# Revit family: LAMP_MOODY G2 800 + ROUND FIXED IP55 REFLECTOR
name_source: partatom
category: Luminarias
revit_build: Autodesk Revit 2015 (Build: 20140606_1530(x64)
units: mm (PartAtom-declared; Revit-internal decimal feet)

## types (9) — shared parameters
Altura reflector = 57 mm
Black reflector code = MORFRD100FX55B
Black reflector datasheet = http://www.lamp.es
Black reflector description = MOODY REF RD FX Ø99 BK.
Black reflector finish = Matt black
Black reflector model = MORFRD100FX55B
Cambio de temperatura de color de luz atenuada = <Ninguno>
Comentarios de tipo = Availability of switching reflector colour when placed in a project.
Core datasheet = http://www.lamp.es
Core description = MOODY CORE 500 VWW MFL
Core diameter = 50 mm  [stored 0.164042 ft]
Fabricante = LAMP
Filtro de color = 16777215
Gear = Electronic
IEE = A++
Installation instructions = https://www.lamp.es
Insulation class = II
LED Lifetime = 50.000 L90 B10
Last update = 28/08/2019
Luminaire type = Indoor - Recessed Downlight
Lámpara = COB LED
MacAdam = 3
Manufacturer URL = http://www.lamp.es
Manufacturer country = Spain
Manufacturer name = LAMP
Material Muelle Emp. = LAMP_Acero genérico
Material Reflector Blanco = LAMP_PC Reflector Moody BL
Material Reflector Cobre = LAMP_PC Reflector Moody CO
Material Reflector Negro = LAMP_PC Reflector Moody NG
Material Reflector Plata = LAMP_PC Reflector Moody GR
Material cristal = Cristal
Model explanation = Availability of switching reflector colour when placed in a project.
Plum = 6 W
Power = 5 W
Power Supply = 220-240V 50/60Hz
Product URL = https://www.lamp.es
Protection rating = IP20
Recessed diameter = 95 mm
Reflector diameter = 100 mm  [stored 0.328084 ft]
Total height = 115 mm  [stored 0.377297 ft]
Total weight = 0.25 kg
Type = COB PHILIPS
UGR = 21
White reflector code = MORFRD100FX55W
White reflector datasheet = http://www.lamp.es
White reflector description = MOODY REF RD FX Ø99 WH.
White reflector finish = Matt white
White reflector model = MORFRD100FX55W
Ángulo de inclinación = 90.00°

## per-type parameters (varying)
| type | Archivo de red fotométrica | CRI | Core model | Core product code | Descripción | Efficacy |
| 2700K FLOOD | MO208FL927TB.IES | 90 | MO208FL927TB | MO208FL927TB | MOODY G2 800 VWW FL TRIAC BK. | 71 lm/W |
| 2700K SPOT | MO208SP927TB.IES | 90 | MO208SP927TB | MO208SP927TB | MOODY G2 800 VWW SP TRIAC BK. | 71 lm/W |
| 2700K WIDE FLOOD | MO208WF927TB.IES | 90 | MO208WF927TB | MO208WF927TB | MOODY G2 800 VWW WFL TRIAC BK. | 71 lm/W |
| 3000K FLOOD | MO208FL830TB.IES | 80 | MO208FL830TB | MO208FL830TB | MOODY G2 800 WW FL TRIAC BK. | 87 lm/W |
| 3000K SPOT | MO208SP830TB.IES | 80 | MO208SP830TB | MO208SP830TB | MOODY G2 800 WW SP TRIAC BK. | 87 lm/W |
| 3000K WIDE FLOOD | MO208WF830TB.IES | 80 | MO208WF830TB | MO208WF830TB | MOODY G2 800 WW WFL TRIAC BK. | 87 lm/W |
| 4000K FLOOD | MO208FL840TB.IES | 80 | MO208FL840TB | MO208FL840TB | MOODY G2 800 NW FL TRIAC BK. | 93 lm/W |
| 4000K SPOT | MO208SP840TB.IES | 80 | MO208SP840TB | MO208SP840TB | MOODY G2 800 NW SP TRIAC BK. | 93 lm/W |
| 4000K WIDE FLOOD | MO208WF840TB.IES | 80 | MO208WF840TB | MO208WF840TB | MOODY G2 800 NW WFL TRIAC BK. | 93 lm/W |

note: [stored X ft] marks values corroborated as IEEE doubles in the binary element streams (Revit-internal decimal feet)

## geometry (parser evidence)
native form markers: Blend x2
no freeform markers — native parametric forms only
